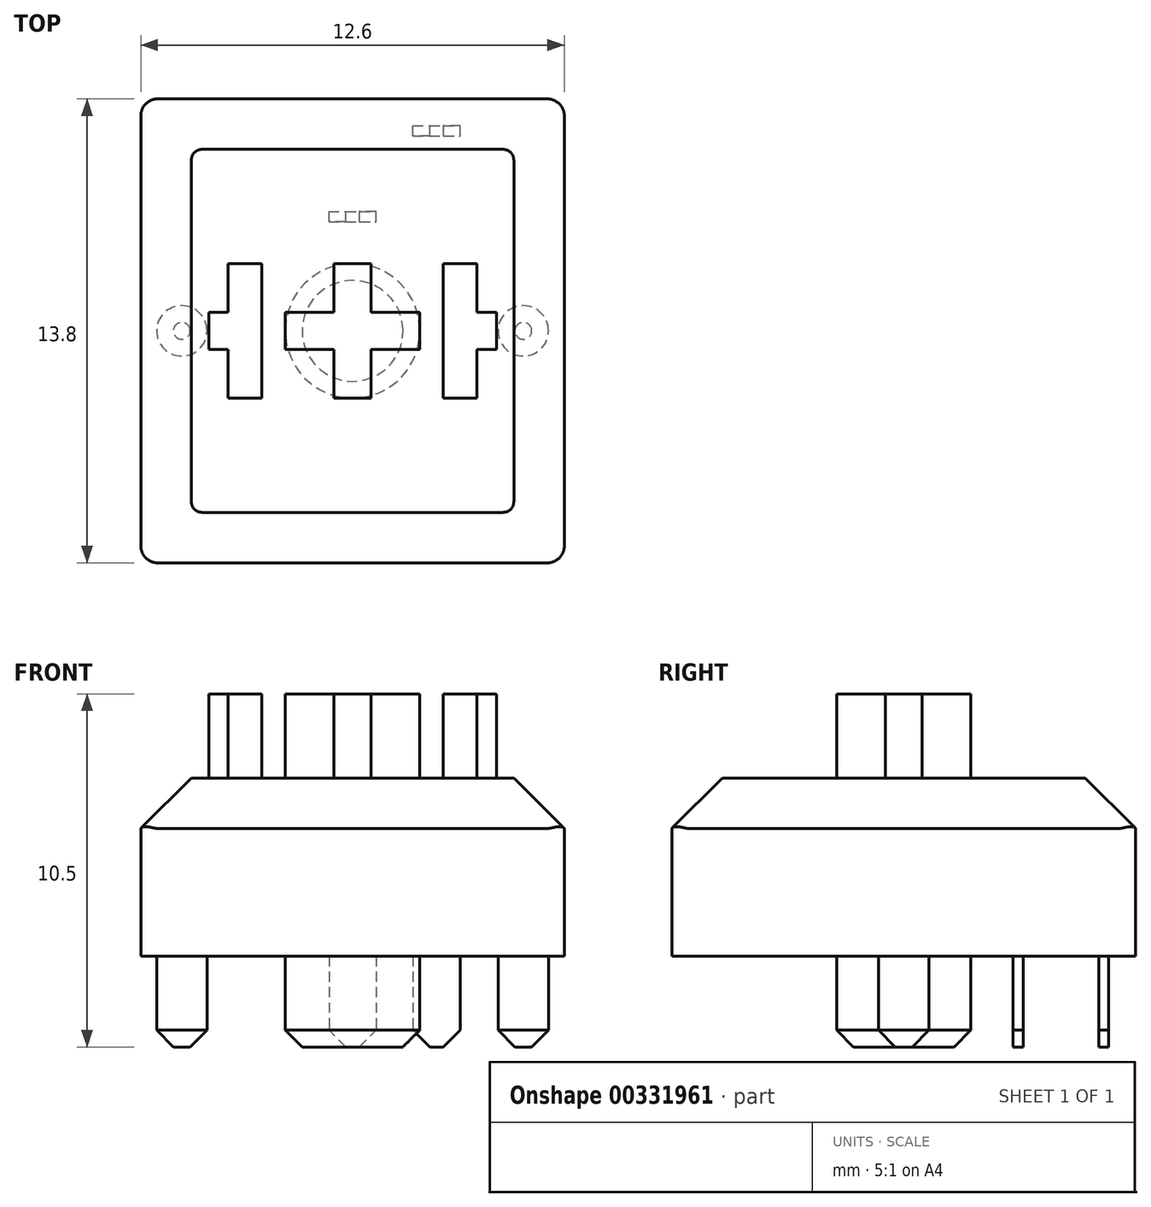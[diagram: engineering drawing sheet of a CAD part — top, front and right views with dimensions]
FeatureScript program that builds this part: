
annotation { "Feature Type Name" : "Feature", "Feature Type Description" : "" }
export const myFeature = defineFeature(function(context is Context, id is Id, definition is map)
    precondition{}
    {
        {
            var Q0;
            Q0=qCreatedBy(makeId("Top.planeOp"),FACE);
            var sketch = newSketch(context, id + "F0", { "sketchPlane" : qUnion([Q0])});
            skLineSegment(sketch, "E0.bottom", {"start": v(-6.3, 6.9) * mm, "end": v(6.3, 6.9) * mm});
            skLineSegment(sketch, "E0.top", {"start": v(-6.3, -6.9) * mm, "end": v(6.3, -6.9) * mm});
            skLineSegment(sketch, "E0.left", {"start": v(-6.3, 6.9) * mm, "end": v(-6.3, -6.9) * mm});
            skLineSegment(sketch, "E0.right", {"start": v(6.3, 6.9) * mm, "end": v(6.3, -6.9) * mm});
            skPoint(sketch, "E1", {"position": v(0, 6.9) * mm});
            skPoint(sketch, "E2", {"position": v(-6.3, 0) * mm});
            skSolve(sketch);
        }
        {
            var Q0;
            Q0 = qSketchRegion(id + "F0", true);
            extrude(context, id + "F1", {"entities" : qUnion([Q0]), "depth" : 5.3 * mm});
        }
        {
            var Q0;
            Q0=makeQuery(id+"F1.opExtrude","CAP_EDGE",EDGE,{"disambiguationData":[OSD([sQuery(id+"F0.wireOp",EDGE,"E0.left")])],"isStart":false});
            var Q1;
            Q1=makeQuery(id+"F1.opExtrude","CAP_EDGE",EDGE,{"disambiguationData":[OSD([sQuery(id+"F0.wireOp",EDGE,"E0.bottom")])],"isStart":false});
            var Q2;
            Q2=makeQuery(id+"F1.opExtrude","CAP_EDGE",EDGE,{"disambiguationData":[OSD([sQuery(id+"F0.wireOp",EDGE,"E0.right")])],"isStart":false});
            var Q3;
            Q3=makeQuery(id+"F1.opExtrude","CAP_EDGE",EDGE,{"disambiguationData":[OSD([sQuery(id+"F0.wireOp",EDGE,"E0.top")])],"isStart":false});
            chamfer(context, id + "F2", {"entities" : qUnion([Q0, Q1, Q2, Q3]), "width" : 1.5 * mm, "tangentPropagation" : true});
        }
        {
            var Q0;
            Q0=makeQuery(id+"F1.opExtrude","SWEPT_EDGE",EDGE,{"disambiguationData":[OSD([sQuery(id+"F0.wireOp",EDGE,"E0.bottom"),sQuery(id+"F0.wireOp",EDGE,"E0.left")])]});
            var Q1;
            Q1=makeQuery(id+"F1.opExtrude","SWEPT_EDGE",EDGE,{"disambiguationData":[OSD([sQuery(id+"F0.wireOp",EDGE,"E0.bottom"),sQuery(id+"F0.wireOp",EDGE,"E0.right")])]});
            var Q2;
            Q2=makeQuery(id+"F1.opExtrude","SWEPT_EDGE",EDGE,{"disambiguationData":[OSD([sQuery(id+"F0.wireOp",EDGE,"E0.top"),sQuery(id+"F0.wireOp",EDGE,"E0.right")])]});
            var Q3;
            Q3=makeQuery(id+"F1.opExtrude","SWEPT_EDGE",EDGE,{"disambiguationData":[OSD([sQuery(id+"F0.wireOp",EDGE,"E0.top"),sQuery(id+"F0.wireOp",EDGE,"E0.left")])]});
            var Q4;
            Q4=makeQuery(id+"F2.opChamfer","BLEND_EDGE",EDGE,{"blendedFrom":[makeQuery(id+"F1.opExtrude","CAP_EDGE",EDGE,{"disambiguationData":[OSD([sQuery(id+"F0.wireOp",EDGE,"E0.bottom")])],"isStart":false}),makeQuery(id+"F1.opExtrude","CAP_EDGE",EDGE,{"disambiguationData":[OSD([sQuery(id+"F0.wireOp",EDGE,"E0.left")])],"isStart":false})],"blendedInto":[]});
            var Q5;
            Q5=makeQuery(id+"F2.opChamfer","BLEND_EDGE",EDGE,{"blendedFrom":[makeQuery(id+"F1.opExtrude","CAP_EDGE",EDGE,{"disambiguationData":[OSD([sQuery(id+"F0.wireOp",EDGE,"E0.bottom")])],"isStart":false}),makeQuery(id+"F1.opExtrude","CAP_EDGE",EDGE,{"disambiguationData":[OSD([sQuery(id+"F0.wireOp",EDGE,"E0.right")])],"isStart":false})],"blendedInto":[]});
            var Q6;
            Q6=makeQuery(id+"F2.opChamfer","BLEND_EDGE",EDGE,{"blendedFrom":[makeQuery(id+"F1.opExtrude","CAP_EDGE",EDGE,{"disambiguationData":[OSD([sQuery(id+"F0.wireOp",EDGE,"E0.top")])],"isStart":false}),makeQuery(id+"F1.opExtrude","CAP_EDGE",EDGE,{"disambiguationData":[OSD([sQuery(id+"F0.wireOp",EDGE,"E0.right")])],"isStart":false})],"blendedInto":[]});
            var Q7;
            Q7=makeQuery(id+"F2.opChamfer","BLEND_EDGE",EDGE,{"blendedFrom":[makeQuery(id+"F1.opExtrude","CAP_EDGE",EDGE,{"disambiguationData":[OSD([sQuery(id+"F0.wireOp",EDGE,"E0.top")])],"isStart":false}),makeQuery(id+"F1.opExtrude","CAP_EDGE",EDGE,{"disambiguationData":[OSD([sQuery(id+"F0.wireOp",EDGE,"E0.left")])],"isStart":false})],"blendedInto":[]});
            fillet(context, id + "F3", {"entities" : qUnion([Q0, Q1, Q2, Q3, Q4, Q5, Q6, Q7]), "radius" : 0.5 * mm, "tangentPropagation" : true, "allowEdgeOverflow" : false});
        }
        {
            var Q0;
            Q0=qCreatedBy(makeId("Top.planeOp"),FACE);
            var sketch = newSketch(context, id + "F4", { "sketchPlane" : qUnion([Q0])});
            skCircle(sketch, "E3", {"center": v(0, 0) * mm, "radius": 2 * mm});
            skCircle(sketch, "E4", {"center": v(-5.08, 0) * mm, "radius": 0.75 * mm});
            skLineSegment(sketch, "E5", {"start": v(0, 7.42) * mm, "end": v(0, 3.01) * mm, "construction": true});
            skCircle(sketch, "E6.MirrorC", {"center": v(5.08, 0) * mm, "radius": 0.75 * mm});
            skSolve(sketch);
        }
        {
            var Q0;
            Q0 = qSketchRegion(id + "F4", true);
            extrude(context, id + "F5", {"entities" : qUnion([Q0]), "operationType" : NewBodyOperationType.ADD, "oppositeDirection" : true, "depth" : 2.7 * mm});
        }
        {
            var Q0;
            Q0=makeQuery(id+"F5.opExtrude","CAP_EDGE",EDGE,{"disambiguationData":[OSD([sQuery(id+"F4.wireOp",EDGE,"E3")])],"isStart":false});
            var Q1;
            Q1=makeQuery(id+"F5.opExtrude","CAP_EDGE",EDGE,{"disambiguationData":[OSD([sQuery(id+"F4.wireOp",EDGE,"E4")])],"isStart":false});
            var Q2;
            Q2=makeQuery(id+"F5.opExtrude","CAP_EDGE",EDGE,{"disambiguationData":[OSD([sQuery(id+"F4.wireOp",EDGE,"E6.MirrorC")])],"isStart":false});
            chamfer(context, id + "F6", {"entities" : qUnion([Q0, Q1, Q2]), "width" : 0.5 * mm, "tangentPropagation" : true});
        }
        {
            var Q0;
            Q0=qCreatedBy(makeId("Front.planeOp"),FACE);
            var sketch = newSketch(context, id + "F7", { "sketchPlane" : qUnion([Q0])});
            skLineSegment(sketch, "E7.bottom", {"start": v(-0.7, 0) * mm, "end": v(0.7, 0) * mm});
            skLineSegment(sketch, "E7.top", {"start": v(-0.7, -2.7) * mm, "end": v(0.7, -2.7) * mm});
            skLineSegment(sketch, "E7.left", {"start": v(-0.7, 0) * mm, "end": v(-0.7, -2.7) * mm});
            skLineSegment(sketch, "E7.right", {"start": v(0.7, 0) * mm, "end": v(0.7, -2.7) * mm});
            skPoint(sketch, "E8", {"position": v(0, -2.7) * mm});
            skSolve(sketch);
        }
        {
            var Q0;
            Q0 = qSketchRegion(id + "F7", true);
            extrude(context, id + "F8", {"entities" : qUnion([Q0]), "endBound" : BoundingType.SYMMETRIC, "depth" : 0.3 * mm});
        }
        {
            var Q0;
            Q0=makeQuery(id+"F8.opExtrude","SWEPT_EDGE",EDGE,{"disambiguationData":[OSD([sQuery(id+"F7.wireOp",EDGE,"E7.top"),sQuery(id+"F7.wireOp",EDGE,"E7.left")])]});
            var Q1;
            Q1=makeQuery(id+"F8.opExtrude","SWEPT_EDGE",EDGE,{"disambiguationData":[OSD([sQuery(id+"F7.wireOp",EDGE,"E7.top"),sQuery(id+"F7.wireOp",EDGE,"E7.right")])]});
            chamfer(context, id + "F9", {"entities" : qUnion([Q0, Q1]), "width" : 0.5 * mm, "tangentPropagation" : true});
        }
        {
            var Q0;
            Q0=makeQuery(id+"F8.opExtrude","SWEPT_BODY",BODY,{"disambiguationData":[OSD([sQuery(id+"F7.wireOp",EDGE,"E7.bottom"),sQuery(id+"F7.wireOp",EDGE,"E7.top"),sQuery(id+"F7.wireOp",EDGE,"E7.left"),sQuery(id+"F7.wireOp",EDGE,"E7.right")])]});
            transform(context, id + "F10", {"entities" : qUnion([Q0]), "transformType" : TransformType.TRANSLATION_3D, "dx" : 0 * mm, "dy" : 3.4 * mm, "dz" : 0 * mm, "makeCopy" : true});
        }
        {
            var Q0;
            Q0=makeQuery(id+"F8.opExtrude","SWEPT_BODY",BODY,{"disambiguationData":[OSD([sQuery(id+"F7.wireOp",EDGE,"E7.bottom"),sQuery(id+"F7.wireOp",EDGE,"E7.top"),sQuery(id+"F7.wireOp",EDGE,"E7.left"),sQuery(id+"F7.wireOp",EDGE,"E7.right")])]});
            transform(context, id + "F11", {"entities" : qUnion([Q0]), "transformType" : TransformType.TRANSLATION_3D, "dx" : 2.5 * mm, "dy" : 5.95 * mm, "dz" : 0 * mm, "makeCopy" : false});
        }
        {
            var Q0;
            Q0=makeQuery(id+"F1.opExtrude","CAP_FACE",FACE,{"disambiguationData":[OSD([sQuery(id+"F0.wireOp",EDGE,"E0.bottom"),sQuery(id+"F0.wireOp",EDGE,"E0.top"),sQuery(id+"F0.wireOp",EDGE,"E0.left"),sQuery(id+"F0.wireOp",EDGE,"E0.right")])],"isStart":false});
            var sketch = newSketch(context, id + "F12", { "sketchPlane" : qUnion([Q0])});
            skLineSegment(sketch, "E9.bottom", {"start": v(0.55, 2) * mm, "end": v(-0.55, 2) * mm});
            skLineSegment(sketch, "E9.top", {"start": v(0.55, -2) * mm, "end": v(-0.55, -2) * mm});
            skLineSegment(sketch, "E9.left", {"start": v(0.55, 2) * mm, "end": v(0.55, -2) * mm});
            skLineSegment(sketch, "E9.right", {"start": v(-0.55, 2) * mm, "end": v(-0.55, -2) * mm});
            skPoint(sketch, "E9.middle", {"position": v(0, 0) * mm});
            skLineSegment(sketch, "E10.bottom", {"start": v(2, 0.55) * mm, "end": v(-2, 0.55) * mm});
            skLineSegment(sketch, "E10.top", {"start": v(2, -0.55) * mm, "end": v(-2, -0.55) * mm});
            skLineSegment(sketch, "E10.left", {"start": v(2, 0.55) * mm, "end": v(2, -0.55) * mm});
            skLineSegment(sketch, "E10.right", {"start": v(-2, 0.55) * mm, "end": v(-2, -0.55) * mm});
            skLineSegment(sketch, "E11.bottom", {"start": v(-2.7, 2) * mm, "end": v(-3.7, 2) * mm});
            skLineSegment(sketch, "E11.top", {"start": v(-2.7, -2) * mm, "end": v(-3.7, -2) * mm});
            skLineSegment(sketch, "E11.left", {"start": v(-2.7, 2) * mm, "end": v(-2.7, -2) * mm});
            skLineSegment(sketch, "E11.right", {"start": v(-3.7, 2) * mm, "end": v(-3.7, -2) * mm});
            skPoint(sketch, "E11.middle", {"position": v(-3.2, 0) * mm});
            skLineSegment(sketch, "E12.bottom", {"start": v(-3.7, 0.55) * mm, "end": v(-4.28, 0.55) * mm});
            skLineSegment(sketch, "E12.top", {"start": v(-3.7, -0.55) * mm, "end": v(-4.28, -0.55) * mm});
            skLineSegment(sketch, "E12.left", {"start": v(-3.7, 0.55) * mm, "end": v(-3.7, -0.55) * mm});
            skLineSegment(sketch, "E12.right", {"start": v(-4.28, 0.55) * mm, "end": v(-4.28, -0.55) * mm});
            skPoint(sketch, "E13", {"position": v(-4.28, 0) * mm});
            skLineSegment(sketch, "E14", {"start": v(0, 4.68) * mm, "end": v(0, 2.33) * mm, "construction": true});
            skLineSegment(sketch, "E15.MirrorCS", {"start": v(3.7, 0.55) * mm, "end": v(3.7, -0.55) * mm});
            skPoint(sketch, "E16.MirrorP", {"position": v(3.2, 0) * mm});
            skLineSegment(sketch, "E17.MirrorCS", {"start": v(3.7, -0.55) * mm, "end": v(4.28, -0.55) * mm});
            skPoint(sketch, "E18.MirrorP", {"position": v(4.28, 0) * mm});
            skLineSegment(sketch, "E19.MirrorCS", {"start": v(3.7, 0.55) * mm, "end": v(4.28, 0.55) * mm});
            skLineSegment(sketch, "E20.MirrorCS", {"start": v(3.7, 2) * mm, "end": v(3.7, -2) * mm});
            skLineSegment(sketch, "E21.MirrorCS", {"start": v(2.7, 2) * mm, "end": v(2.7, -2) * mm});
            skLineSegment(sketch, "E22.MirrorCS", {"start": v(4.28, 0.55) * mm, "end": v(4.28, -0.55) * mm});
            skLineSegment(sketch, "E23.MirrorCS", {"start": v(2.7, -2) * mm, "end": v(3.7, -2) * mm});
            skLineSegment(sketch, "E24.MirrorCS", {"start": v(2.7, 2) * mm, "end": v(3.7, 2) * mm});
            skSolve(sketch);
        }
        {
            var Q0;
            Q0 = qSketchRegion(id + "F12", true);
            extrude(context, id + "F13", {"entities" : qUnion([Q0]), "operationType" : NewBodyOperationType.ADD, "depth" : 2.5 * mm});
        }
    });
